# Revit family: Ленточный арочный зенитный фонарь M8CITY_А_ДЫМ_1_люк_2_растра_2017
name_source: partatom
category: Оборудование
revit_build: Autodesk Revit 2017 (Build: 20170118_1100(x64)
units: mm (PartAtom-declared; Revit-internal decimal feet)

## family parameters
Всегда вертикально = Нет
Общий = Нет
Основа = Крыша
При загрузке вырезать с полостями = Нет
Размер круглого соединителя = Использовать диаметр
Тип детали = Нормальный
Точка расчета площади = Нет

## types (1)
- Зенитный фонарь M8CITY Л-А-1 люк на 2 растра
    ADSK_Завод-изготовитель = ООО ''Завод М8 Сити''
    ADSK_Код изделия = ТУ BY 191302027.002-2013
    ADSK_Количество = 1
    ADSK_Обозначение = M8CITY
    ADSK_Размер_Высота = 300 мм
    ADSK_Размер_Длина = 8500 мм
    ADSK_Размер_Ширина = 3500 мм
    Table 1 = Описание
    Table 2 = Расчет
    Table 3 = Маркировка
    URL = www.m8city.by
    Высота = 373 мм
    Высота основания = 300 мм
    Длина = 8500 мм
    Длина ПК = 3765 мм
    Длина проёма = 8500 мм
    Длина проёма ввод = 8500 мм
    Длина створки = 1600 мм
    Длина створки ном = 1600 мм
    Заполнение = 1
    Количество арок = 4
    Типовой растр = 1060 мм
    Шаг двойного растра = 2120 мм
    Шаг типовой = 1060 мм
    Ширина = 3500 мм
    Ширина проёма = 3500 мм
    Ширина проёма ввод = 3500 мм
